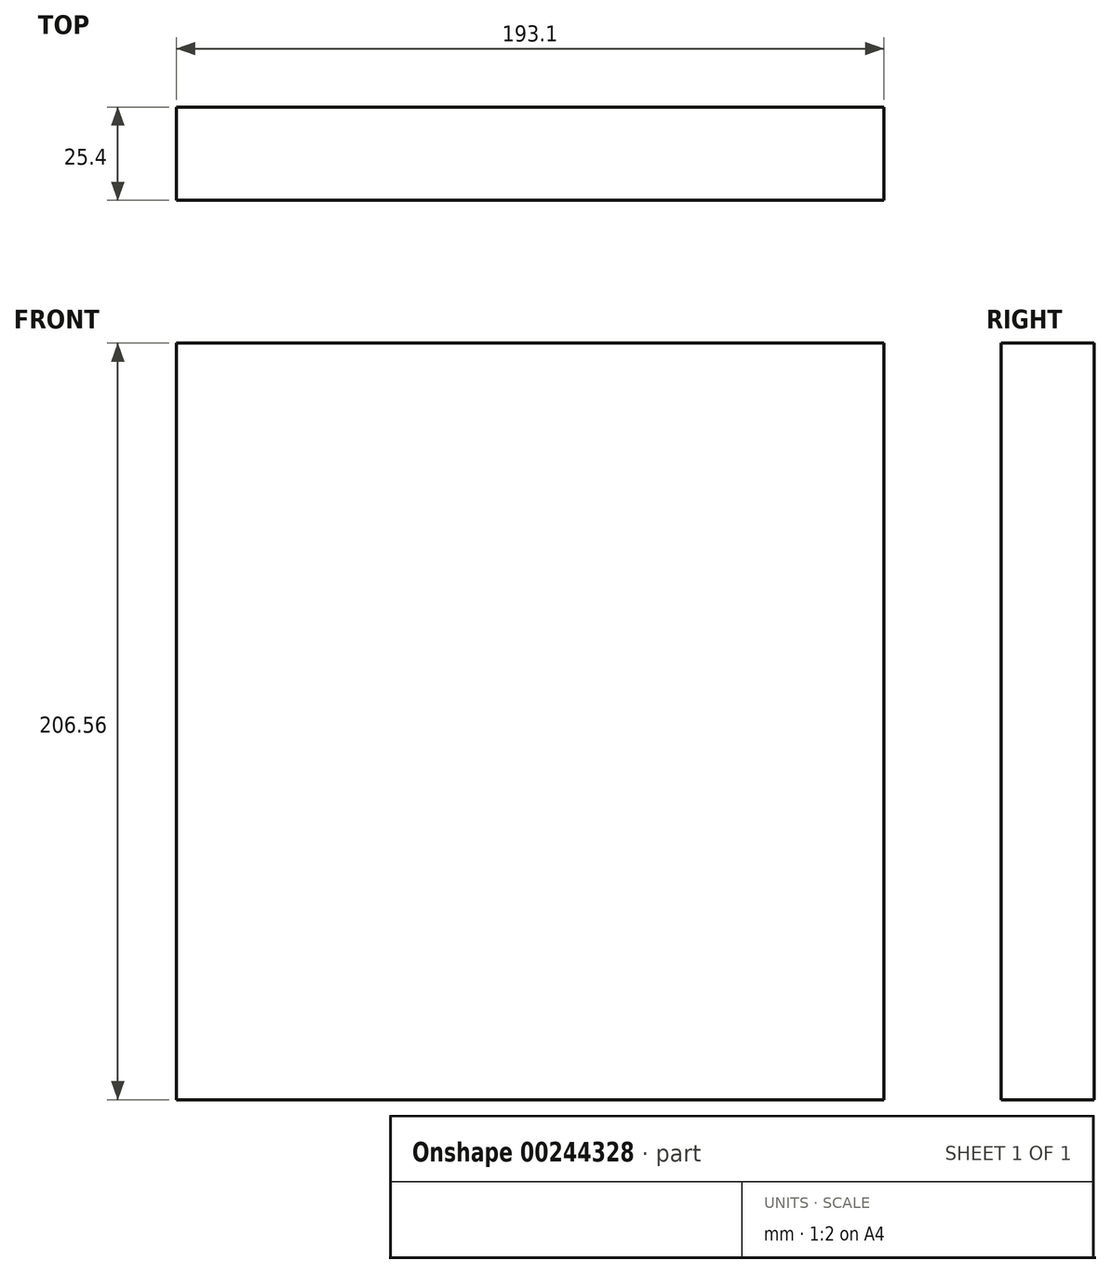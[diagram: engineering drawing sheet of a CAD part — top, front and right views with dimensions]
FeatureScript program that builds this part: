
annotation { "Feature Type Name" : "Feature", "Feature Type Description" : "" }
export const myFeature = defineFeature(function(context is Context, id is Id, definition is map)
    precondition{}
    {
        {
            var Q0;
            Q0=qCreatedBy(makeId("Front.planeOp"),FACE);
            var sketch = newSketch(context, id + "F0", { "sketchPlane" : qUnion([Q0])});
            skLineSegment(sketch, "E0.bottom", {"start": v(96.55, -103.28) * mm, "end": v(-96.55, -103.28) * mm});
            skLineSegment(sketch, "E0.top", {"start": v(96.55, 103.28) * mm, "end": v(-96.55, 103.28) * mm});
            skLineSegment(sketch, "E0.left", {"start": v(96.55, -103.28) * mm, "end": v(96.55, 103.28) * mm});
            skLineSegment(sketch, "E0.right", {"start": v(-96.55, -103.28) * mm, "end": v(-96.55, 103.28) * mm});
            skPoint(sketch, "E0.middle", {"position": v(0, 0) * mm});
            skCircle(sketch, "E1", {"center": v(0, 0) * mm, "radius": 67.9 * mm});
            skSolve(sketch);
        }
        {
            var Q0;
            Q0=makeQuery(id+"F0.imprint","IMPRINT",FACE,{"disambiguationData":[TD([[makeQuery(id+"F0.imprint","IMPRINT",EDGE,{"derivedFrom":sQuery(id+"F0.wireOp",EDGE,"E1")}),1.0]])]});
            var Q1;
            Q1=makeQuery(id+"F0.imprint","IMPRINT",FACE,{"disambiguationData":[TD([[makeQuery(id+"F0.imprint","IMPRINT",EDGE,{"derivedFrom":sQuery(id+"F0.wireOp",EDGE,"E0.bottom")}),-1.0]])]});
            extrude(context, id + "F1", {"entities" : qUnion([Q0, Q1]), "depth" : 25.4 * mm});
        }
    });
